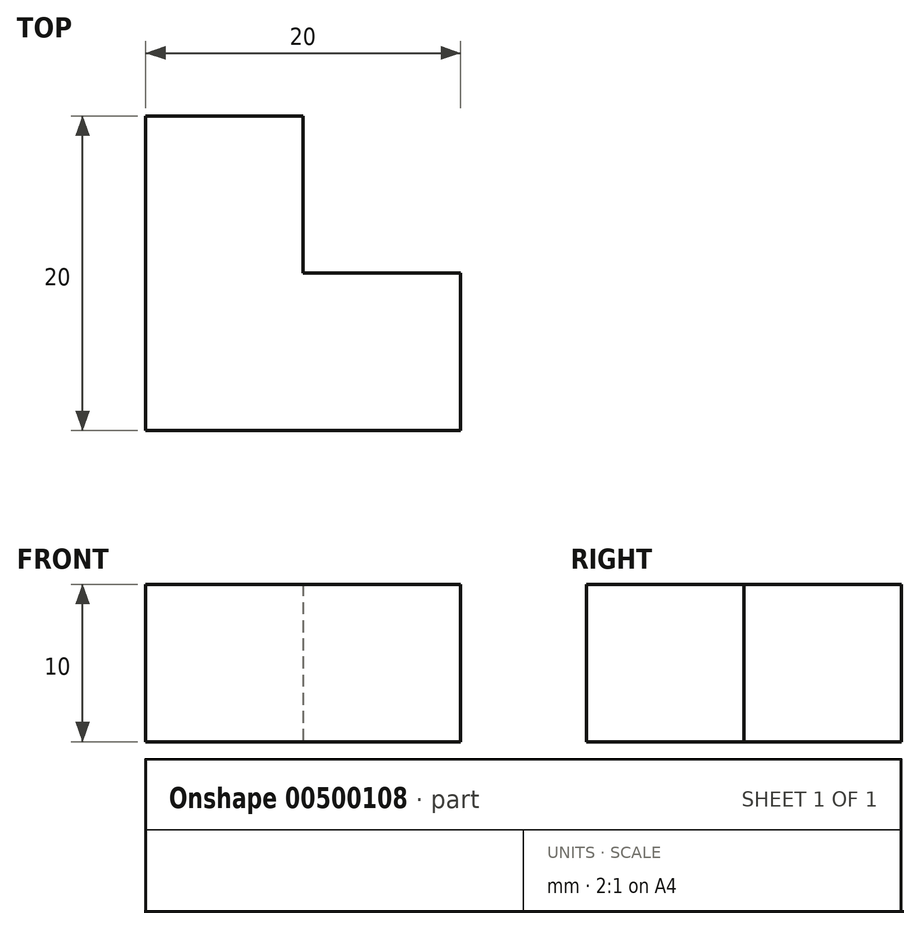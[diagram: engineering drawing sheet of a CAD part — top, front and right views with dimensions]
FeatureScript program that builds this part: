
annotation { "Feature Type Name" : "Feature", "Feature Type Description" : "" }
export const myFeature = defineFeature(function(context is Context, id is Id, definition is map)
    precondition{}
    {
        {
            var Q0;
            Q0=qCreatedBy(makeId("Top.planeOp"),FACE);
            var sketch = newSketch(context, id + "F0", { "sketchPlane" : qUnion([Q0])});
            skLineSegment(sketch, "E0", {"start": v(-57.27, 16.94) * mm, "end": v(-37.27, 16.94) * mm});
            skLineSegment(sketch, "E1", {"start": v(-37.27, 16.94) * mm, "end": v(-37.27, 26.94) * mm});
            skLineSegment(sketch, "E2", {"start": v(-37.27, 26.94) * mm, "end": v(-47.27, 26.94) * mm});
            skLineSegment(sketch, "E3", {"start": v(-47.27, 26.94) * mm, "end": v(-47.27, 36.94) * mm});
            skLineSegment(sketch, "E4", {"start": v(-47.27, 36.94) * mm, "end": v(-57.27, 36.94) * mm});
            skLineSegment(sketch, "E5", {"start": v(-57.27, 36.94) * mm, "end": v(-57.27, 16.94) * mm});
            skSolve(sketch);
        }
        {
            var Q0;
            Q0=makeQuery(id+"F0.imprint","IMPRINT",FACE,{"disambiguationData":[TD([[makeQuery(id+"F0.imprint","IMPRINT",EDGE,{"derivedFrom":sQuery(id+"F0.wireOp",EDGE,"E0")}),1.0]])]});
            extrude(context, id + "F1", {"entities" : qUnion([Q0]), "depth" : 10 * mm});
        }
    });
